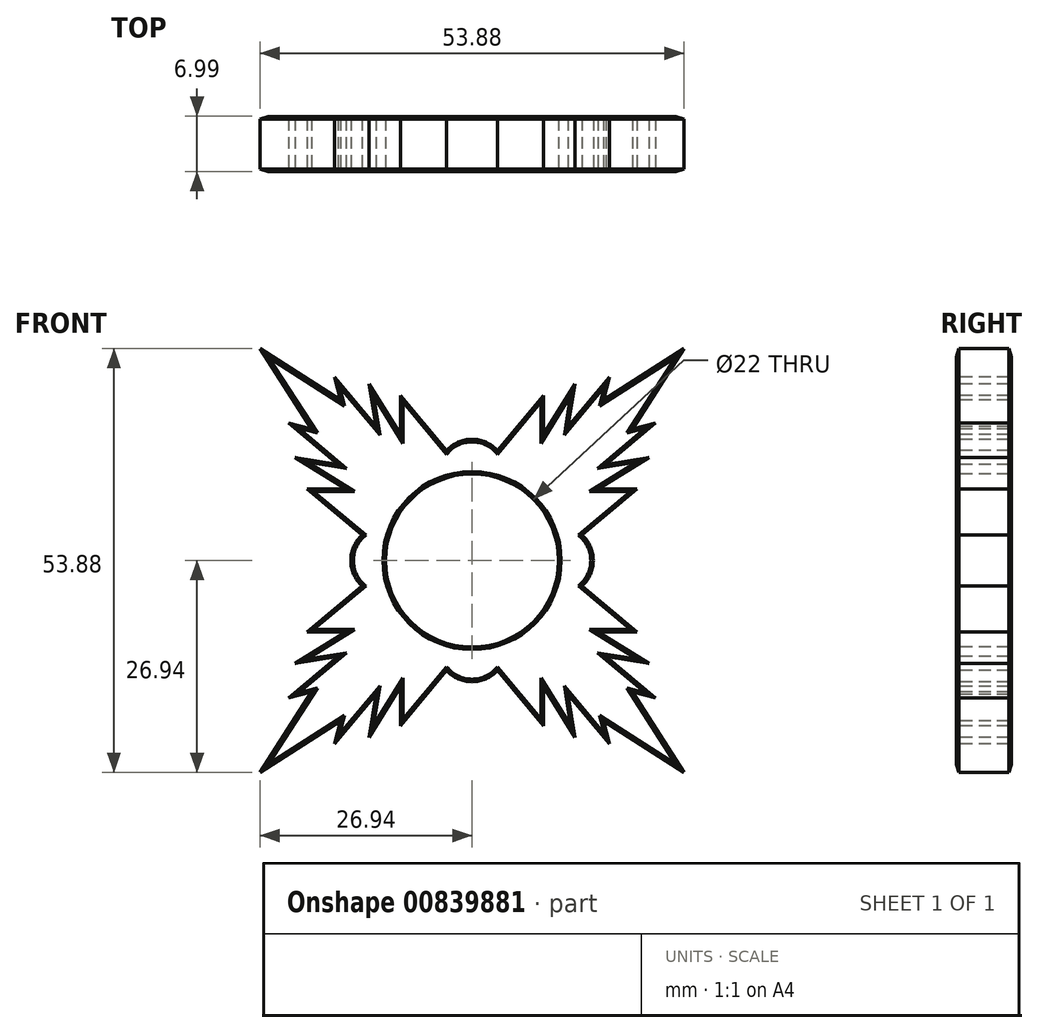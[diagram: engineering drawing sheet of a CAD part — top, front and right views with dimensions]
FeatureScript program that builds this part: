
annotation { "Feature Type Name" : "Feature", "Feature Type Description" : "" }
export const myFeature = defineFeature(function(context is Context, id is Id, definition is map)
    precondition{}
    {
        {
            var Q0;
            Q0=qCreatedBy(makeId("Front.planeOp"),FACE);
            var sketch = newSketch(context, id + "F0", { "sketchPlane" : qUnion([Q0])});
            skLineSegment(sketch, "E0.bottom", {"start": v(26.94, 26.94) * mm, "end": v(-26.94, 26.94) * mm});
            skLineSegment(sketch, "E0.top", {"start": v(26.94, -26.94) * mm, "end": v(-26.94, -26.94) * mm});
            skLineSegment(sketch, "E0.left", {"start": v(26.94, 26.94) * mm, "end": v(26.94, -26.94) * mm});
            skLineSegment(sketch, "E0.right", {"start": v(-26.94, 26.94) * mm, "end": v(-26.94, -26.94) * mm});
            skPoint(sketch, "E0.middle", {"position": v(0, 0) * mm});
            skLineSegment(sketch, "E1", {"start": v(-26.94, 26.94) * mm, "end": v(26.94, -26.94) * mm, "construction": true});
            skLineSegment(sketch, "E2", {"start": v(26.94, 26.94) * mm, "end": v(-26.94, -26.94) * mm, "construction": true});
            skLineSegment(sketch, "E3", {"start": v(0, 26.94) * mm, "end": v(0, -26.94) * mm, "construction": true});
            skLineSegment(sketch, "E4", {"start": v(-26.94, 0) * mm, "end": v(26.94, 0) * mm, "construction": true});
            skCircle(sketch, "E5", {"center": v(0, 0) * mm, "radius": 11 * mm});
            skLineSegment(sketch, "E6", {"start": v(26.94, 26.94) * mm, "end": v(20.36, 16.7) * mm});
            skLineSegment(sketch, "E7", {"start": v(20.36, 16.7) * mm, "end": v(23.3, 17.48) * mm});
            skLineSegment(sketch, "E8", {"start": v(23.3, 17.48) * mm, "end": v(17.02, 12.2) * mm});
            skLineSegment(sketch, "E9", {"start": v(17.02, 12.2) * mm, "end": v(22.45, 13.06) * mm});
            skLineSegment(sketch, "E10", {"start": v(22.45, 13.06) * mm, "end": v(16.02, 9.1) * mm});
            skLineSegment(sketch, "E11", {"start": v(16.02, 9.1) * mm, "end": v(20.98, 9.1) * mm});
            skLineSegment(sketch, "E12", {"start": v(20.98, 9.1) * mm, "end": v(13.98, 3.23) * mm});
            skArc(sketch, "E13", {"start": v(15.4, 0) * mm, "mid": v(15.03, 1.76) * mm, "end": v(13.98, 3.23) * mm});
            skLineSegment(sketch, "E14.MirrorCS", {"start": v(26.94, 26.94) * mm, "end": v(16.7, 20.36) * mm});
            skLineSegment(sketch, "E15.MirrorCS", {"start": v(16.7, 20.36) * mm, "end": v(17.48, 23.3) * mm});
            skLineSegment(sketch, "E16.MirrorCS", {"start": v(17.48, 23.3) * mm, "end": v(12.2, 17.02) * mm});
            skLineSegment(sketch, "E17.MirrorCS", {"start": v(12.2, 17.02) * mm, "end": v(13.06, 22.45) * mm});
            skLineSegment(sketch, "E18.MirrorCS", {"start": v(13.06, 22.45) * mm, "end": v(9.1, 16.02) * mm});
            skLineSegment(sketch, "E19.MirrorCS", {"start": v(9.1, 16.02) * mm, "end": v(9.1, 20.98) * mm});
            skLineSegment(sketch, "E20.MirrorCS", {"start": v(9.1, 20.98) * mm, "end": v(3.23, 13.98) * mm});
            skArc(sketch, "E21.MirrorCS", {"start": v(0, 15.4) * mm, "mid": v(1.76, 15.03) * mm, "end": v(3.23, 13.98) * mm});
            skArc(sketch, "E22.MirrorCS", {"start": v(15.4, 0) * mm, "mid": v(15.03, -1.76) * mm, "end": v(13.98, -3.23) * mm});
            skLineSegment(sketch, "E23.MirrorCS", {"start": v(20.98, -9.1) * mm, "end": v(13.98, -3.23) * mm});
            skLineSegment(sketch, "E24.MirrorCS", {"start": v(16.02, -9.1) * mm, "end": v(20.98, -9.1) * mm});
            skLineSegment(sketch, "E25.MirrorCS", {"start": v(22.45, -13.06) * mm, "end": v(16.02, -9.1) * mm});
            skLineSegment(sketch, "E26.MirrorCS", {"start": v(17.02, -12.2) * mm, "end": v(22.45, -13.06) * mm});
            skLineSegment(sketch, "E27.MirrorCS", {"start": v(23.3, -17.48) * mm, "end": v(17.02, -12.2) * mm});
            skLineSegment(sketch, "E28.MirrorCS", {"start": v(20.36, -16.7) * mm, "end": v(23.3, -17.48) * mm});
            skLineSegment(sketch, "E29.MirrorCS", {"start": v(26.94, -26.94) * mm, "end": v(20.36, -16.7) * mm});
            skLineSegment(sketch, "E30.MirrorCS", {"start": v(26.94, -26.94) * mm, "end": v(16.7, -20.36) * mm});
            skLineSegment(sketch, "E31.MirrorCS", {"start": v(16.7, -20.36) * mm, "end": v(17.48, -23.3) * mm});
            skLineSegment(sketch, "E32.MirrorCS", {"start": v(17.48, -23.3) * mm, "end": v(12.2, -17.02) * mm});
            skLineSegment(sketch, "E33.MirrorCS", {"start": v(12.2, -17.02) * mm, "end": v(13.06, -22.45) * mm});
            skLineSegment(sketch, "E34.MirrorCS", {"start": v(13.06, -22.45) * mm, "end": v(9.1, -16.02) * mm});
            skLineSegment(sketch, "E35.MirrorCS", {"start": v(9.1, -16.02) * mm, "end": v(9.1, -20.98) * mm});
            skLineSegment(sketch, "E36.MirrorCS", {"start": v(9.1, -20.98) * mm, "end": v(3.23, -13.98) * mm});
            skArc(sketch, "E37.MirrorCS", {"start": v(0, -15.4) * mm, "mid": v(1.76, -15.03) * mm, "end": v(3.23, -13.98) * mm});
            skArc(sketch, "E38.MirrorCS", {"start": v(0, 15.4) * mm, "mid": v(-1.76, 15.03) * mm, "end": v(-3.23, 13.98) * mm});
            skLineSegment(sketch, "E39.MirrorCS", {"start": v(-9.1, 20.98) * mm, "end": v(-3.23, 13.98) * mm});
            skLineSegment(sketch, "E40.MirrorCS", {"start": v(-9.1, 16.02) * mm, "end": v(-9.1, 20.98) * mm});
            skLineSegment(sketch, "E41.MirrorCS", {"start": v(-13.06, 22.45) * mm, "end": v(-9.1, 16.02) * mm});
            skLineSegment(sketch, "E42.MirrorCS", {"start": v(-12.2, 17.02) * mm, "end": v(-13.06, 22.45) * mm});
            skLineSegment(sketch, "E43.MirrorCS", {"start": v(-17.48, 23.3) * mm, "end": v(-12.2, 17.02) * mm});
            skLineSegment(sketch, "E44.MirrorCS", {"start": v(-16.7, 20.36) * mm, "end": v(-17.48, 23.3) * mm});
            skLineSegment(sketch, "E45.MirrorCS", {"start": v(-26.94, 26.94) * mm, "end": v(-16.7, 20.36) * mm});
            skLineSegment(sketch, "E46.MirrorCS", {"start": v(-26.94, 26.94) * mm, "end": v(-20.36, 16.7) * mm});
            skLineSegment(sketch, "E47.MirrorCS", {"start": v(-20.36, 16.7) * mm, "end": v(-23.3, 17.48) * mm});
            skLineSegment(sketch, "E48.MirrorCS", {"start": v(-23.3, 17.48) * mm, "end": v(-17.02, 12.2) * mm});
            skLineSegment(sketch, "E49.MirrorCS", {"start": v(-17.02, 12.2) * mm, "end": v(-22.45, 13.06) * mm});
            skLineSegment(sketch, "E50.MirrorCS", {"start": v(-22.45, 13.06) * mm, "end": v(-16.02, 9.1) * mm});
            skLineSegment(sketch, "E51.MirrorCS", {"start": v(-16.02, 9.1) * mm, "end": v(-20.98, 9.1) * mm});
            skLineSegment(sketch, "E52.MirrorCS", {"start": v(-20.98, 9.1) * mm, "end": v(-13.98, 3.23) * mm});
            skArc(sketch, "E53.MirrorCS", {"start": v(-15.4, 0) * mm, "mid": v(-15.03, 1.76) * mm, "end": v(-13.98, 3.23) * mm});
            skArc(sketch, "E54.MirrorCS", {"start": v(-15.4, 0) * mm, "mid": v(-15.03, -1.76) * mm, "end": v(-13.98, -3.23) * mm});
            skLineSegment(sketch, "E55.MirrorCS", {"start": v(-20.98, -9.1) * mm, "end": v(-13.98, -3.23) * mm});
            skLineSegment(sketch, "E56.MirrorCS", {"start": v(-16.02, -9.1) * mm, "end": v(-20.98, -9.1) * mm});
            skLineSegment(sketch, "E57.MirrorCS", {"start": v(-22.45, -13.06) * mm, "end": v(-16.02, -9.1) * mm});
            skLineSegment(sketch, "E58.MirrorCS", {"start": v(-17.02, -12.2) * mm, "end": v(-22.45, -13.06) * mm});
            skLineSegment(sketch, "E59.MirrorCS", {"start": v(-23.3, -17.48) * mm, "end": v(-17.02, -12.2) * mm});
            skLineSegment(sketch, "E60.MirrorCS", {"start": v(-20.36, -16.7) * mm, "end": v(-23.3, -17.48) * mm});
            skLineSegment(sketch, "E61.MirrorCS", {"start": v(-26.94, -26.94) * mm, "end": v(-20.36, -16.7) * mm});
            skLineSegment(sketch, "E62.MirrorCS", {"start": v(-26.94, -26.94) * mm, "end": v(-16.7, -20.36) * mm});
            skLineSegment(sketch, "E63.MirrorCS", {"start": v(-16.7, -20.36) * mm, "end": v(-17.48, -23.3) * mm});
            skLineSegment(sketch, "E64.MirrorCS", {"start": v(-17.48, -23.3) * mm, "end": v(-12.2, -17.02) * mm});
            skLineSegment(sketch, "E65.MirrorCS", {"start": v(-12.2, -17.02) * mm, "end": v(-13.06, -22.45) * mm});
            skLineSegment(sketch, "E66.MirrorCS", {"start": v(-13.06, -22.45) * mm, "end": v(-9.1, -16.02) * mm});
            skLineSegment(sketch, "E67.MirrorCS", {"start": v(-9.1, -16.02) * mm, "end": v(-9.1, -20.98) * mm});
            skLineSegment(sketch, "E68.MirrorCS", {"start": v(-9.1, -20.98) * mm, "end": v(-3.23, -13.98) * mm});
            skArc(sketch, "E69.MirrorCS", {"start": v(0, -15.4) * mm, "mid": v(-1.76, -15.03) * mm, "end": v(-3.23, -13.98) * mm});
            skSolve(sketch);
        }
        {
            var Q0;
            Q0=makeQuery(id+"F0.imprint","IMPRINT",FACE,{"disambiguationData":[TD([[makeQuery(id+"F0.imprint","IMPRINT",EDGE,{"derivedFrom":sQuery(id+"F0.wireOp",EDGE,"E5")}),-1.0]])]});
            extrude(context, id + "F1", {"entities" : qUnion([Q0]), "oppositeDirection" : true, "depth" : 7 * mm, "offsetDistance" : 25.4 * mm});
        }
        {
            var Q0;
            Q0=makeQuery(id+"F1.opExtrude","CAP_FACE",FACE,{"disambiguationData":[OSD([sQuery(id+"F0.wireOp",EDGE,"E5"),sQuery(id+"F0.wireOp",EDGE,"E6"),sQuery(id+"F0.wireOp",EDGE,"E7"),sQuery(id+"F0.wireOp",EDGE,"E8"),sQuery(id+"F0.wireOp",EDGE,"E9"),sQuery(id+"F0.wireOp",EDGE,"E10"),sQuery(id+"F0.wireOp",EDGE,"E11"),sQuery(id+"F0.wireOp",EDGE,"E12"),sQuery(id+"F0.wireOp",EDGE,"E13"),sQuery(id+"F0.wireOp",EDGE,"E14.MirrorCS"),sQuery(id+"F0.wireOp",EDGE,"E15.MirrorCS"),sQuery(id+"F0.wireOp",EDGE,"E16.MirrorCS"),sQuery(id+"F0.wireOp",EDGE,"E17.MirrorCS"),sQuery(id+"F0.wireOp",EDGE,"E18.MirrorCS"),sQuery(id+"F0.wireOp",EDGE,"E19.MirrorCS"),sQuery(id+"F0.wireOp",EDGE,"E20.MirrorCS"),sQuery(id+"F0.wireOp",EDGE,"E21.MirrorCS"),sQuery(id+"F0.wireOp",EDGE,"E22.MirrorCS"),sQuery(id+"F0.wireOp",EDGE,"E23.MirrorCS"),sQuery(id+"F0.wireOp",EDGE,"E24.MirrorCS"),sQuery(id+"F0.wireOp",EDGE,"E25.MirrorCS"),sQuery(id+"F0.wireOp",EDGE,"E26.MirrorCS"),sQuery(id+"F0.wireOp",EDGE,"E27.MirrorCS"),sQuery(id+"F0.wireOp",EDGE,"E28.MirrorCS"),sQuery(id+"F0.wireOp",EDGE,"E29.MirrorCS"),sQuery(id+"F0.wireOp",EDGE,"E30.MirrorCS"),sQuery(id+"F0.wireOp",EDGE,"E31.MirrorCS"),sQuery(id+"F0.wireOp",EDGE,"E32.MirrorCS"),sQuery(id+"F0.wireOp",EDGE,"E33.MirrorCS"),sQuery(id+"F0.wireOp",EDGE,"E34.MirrorCS"),sQuery(id+"F0.wireOp",EDGE,"E35.MirrorCS"),sQuery(id+"F0.wireOp",EDGE,"E36.MirrorCS"),sQuery(id+"F0.wireOp",EDGE,"E37.MirrorCS"),sQuery(id+"F0.wireOp",EDGE,"E38.MirrorCS"),sQuery(id+"F0.wireOp",EDGE,"E39.MirrorCS"),sQuery(id+"F0.wireOp",EDGE,"E40.MirrorCS"),sQuery(id+"F0.wireOp",EDGE,"E41.MirrorCS"),sQuery(id+"F0.wireOp",EDGE,"E42.MirrorCS"),sQuery(id+"F0.wireOp",EDGE,"E43.MirrorCS"),sQuery(id+"F0.wireOp",EDGE,"E44.MirrorCS"),sQuery(id+"F0.wireOp",EDGE,"E45.MirrorCS"),sQuery(id+"F0.wireOp",EDGE,"E46.MirrorCS"),sQuery(id+"F0.wireOp",EDGE,"E47.MirrorCS"),sQuery(id+"F0.wireOp",EDGE,"E48.MirrorCS"),sQuery(id+"F0.wireOp",EDGE,"E49.MirrorCS"),sQuery(id+"F0.wireOp",EDGE,"E50.MirrorCS"),sQuery(id+"F0.wireOp",EDGE,"E51.MirrorCS"),sQuery(id+"F0.wireOp",EDGE,"E52.MirrorCS"),sQuery(id+"F0.wireOp",EDGE,"E53.MirrorCS"),sQuery(id+"F0.wireOp",EDGE,"E54.MirrorCS"),sQuery(id+"F0.wireOp",EDGE,"E55.MirrorCS"),sQuery(id+"F0.wireOp",EDGE,"E56.MirrorCS"),sQuery(id+"F0.wireOp",EDGE,"E57.MirrorCS"),sQuery(id+"F0.wireOp",EDGE,"E58.MirrorCS"),sQuery(id+"F0.wireOp",EDGE,"E59.MirrorCS"),sQuery(id+"F0.wireOp",EDGE,"E60.MirrorCS"),sQuery(id+"F0.wireOp",EDGE,"E61.MirrorCS"),sQuery(id+"F0.wireOp",EDGE,"E62.MirrorCS"),sQuery(id+"F0.wireOp",EDGE,"E63.MirrorCS"),sQuery(id+"F0.wireOp",EDGE,"E64.MirrorCS"),sQuery(id+"F0.wireOp",EDGE,"E65.MirrorCS"),sQuery(id+"F0.wireOp",EDGE,"E66.MirrorCS"),sQuery(id+"F0.wireOp",EDGE,"E67.MirrorCS"),sQuery(id+"F0.wireOp",EDGE,"E68.MirrorCS"),sQuery(id+"F0.wireOp",EDGE,"E69.MirrorCS")])],"isStart":true});
            chamfer(context, id + "F2", {"entities" : qUnion([Q0]), "width" : 0.32 * mm, "tangentPropagation" : true});
        }
        {
            var Q0;
            Q0=makeQuery(id+"F1.opExtrude","CAP_FACE",FACE,{"disambiguationData":[OSD([sQuery(id+"F0.wireOp",EDGE,"E5"),sQuery(id+"F0.wireOp",EDGE,"E6"),sQuery(id+"F0.wireOp",EDGE,"E7"),sQuery(id+"F0.wireOp",EDGE,"E8"),sQuery(id+"F0.wireOp",EDGE,"E9"),sQuery(id+"F0.wireOp",EDGE,"E10"),sQuery(id+"F0.wireOp",EDGE,"E11"),sQuery(id+"F0.wireOp",EDGE,"E12"),sQuery(id+"F0.wireOp",EDGE,"E13"),sQuery(id+"F0.wireOp",EDGE,"E14.MirrorCS"),sQuery(id+"F0.wireOp",EDGE,"E15.MirrorCS"),sQuery(id+"F0.wireOp",EDGE,"E16.MirrorCS"),sQuery(id+"F0.wireOp",EDGE,"E17.MirrorCS"),sQuery(id+"F0.wireOp",EDGE,"E18.MirrorCS"),sQuery(id+"F0.wireOp",EDGE,"E19.MirrorCS"),sQuery(id+"F0.wireOp",EDGE,"E20.MirrorCS"),sQuery(id+"F0.wireOp",EDGE,"E21.MirrorCS"),sQuery(id+"F0.wireOp",EDGE,"E22.MirrorCS"),sQuery(id+"F0.wireOp",EDGE,"E23.MirrorCS"),sQuery(id+"F0.wireOp",EDGE,"E24.MirrorCS"),sQuery(id+"F0.wireOp",EDGE,"E25.MirrorCS"),sQuery(id+"F0.wireOp",EDGE,"E26.MirrorCS"),sQuery(id+"F0.wireOp",EDGE,"E27.MirrorCS"),sQuery(id+"F0.wireOp",EDGE,"E28.MirrorCS"),sQuery(id+"F0.wireOp",EDGE,"E29.MirrorCS"),sQuery(id+"F0.wireOp",EDGE,"E30.MirrorCS"),sQuery(id+"F0.wireOp",EDGE,"E31.MirrorCS"),sQuery(id+"F0.wireOp",EDGE,"E32.MirrorCS"),sQuery(id+"F0.wireOp",EDGE,"E33.MirrorCS"),sQuery(id+"F0.wireOp",EDGE,"E34.MirrorCS"),sQuery(id+"F0.wireOp",EDGE,"E35.MirrorCS"),sQuery(id+"F0.wireOp",EDGE,"E36.MirrorCS"),sQuery(id+"F0.wireOp",EDGE,"E37.MirrorCS"),sQuery(id+"F0.wireOp",EDGE,"E38.MirrorCS"),sQuery(id+"F0.wireOp",EDGE,"E39.MirrorCS"),sQuery(id+"F0.wireOp",EDGE,"E40.MirrorCS"),sQuery(id+"F0.wireOp",EDGE,"E41.MirrorCS"),sQuery(id+"F0.wireOp",EDGE,"E42.MirrorCS"),sQuery(id+"F0.wireOp",EDGE,"E43.MirrorCS"),sQuery(id+"F0.wireOp",EDGE,"E44.MirrorCS"),sQuery(id+"F0.wireOp",EDGE,"E45.MirrorCS"),sQuery(id+"F0.wireOp",EDGE,"E46.MirrorCS"),sQuery(id+"F0.wireOp",EDGE,"E47.MirrorCS"),sQuery(id+"F0.wireOp",EDGE,"E48.MirrorCS"),sQuery(id+"F0.wireOp",EDGE,"E49.MirrorCS"),sQuery(id+"F0.wireOp",EDGE,"E50.MirrorCS"),sQuery(id+"F0.wireOp",EDGE,"E51.MirrorCS"),sQuery(id+"F0.wireOp",EDGE,"E52.MirrorCS"),sQuery(id+"F0.wireOp",EDGE,"E53.MirrorCS"),sQuery(id+"F0.wireOp",EDGE,"E54.MirrorCS"),sQuery(id+"F0.wireOp",EDGE,"E55.MirrorCS"),sQuery(id+"F0.wireOp",EDGE,"E56.MirrorCS"),sQuery(id+"F0.wireOp",EDGE,"E57.MirrorCS"),sQuery(id+"F0.wireOp",EDGE,"E58.MirrorCS"),sQuery(id+"F0.wireOp",EDGE,"E59.MirrorCS"),sQuery(id+"F0.wireOp",EDGE,"E60.MirrorCS"),sQuery(id+"F0.wireOp",EDGE,"E61.MirrorCS"),sQuery(id+"F0.wireOp",EDGE,"E62.MirrorCS"),sQuery(id+"F0.wireOp",EDGE,"E63.MirrorCS"),sQuery(id+"F0.wireOp",EDGE,"E64.MirrorCS"),sQuery(id+"F0.wireOp",EDGE,"E65.MirrorCS"),sQuery(id+"F0.wireOp",EDGE,"E66.MirrorCS"),sQuery(id+"F0.wireOp",EDGE,"E67.MirrorCS"),sQuery(id+"F0.wireOp",EDGE,"E68.MirrorCS"),sQuery(id+"F0.wireOp",EDGE,"E69.MirrorCS")])],"isStart":false});
            chamfer(context, id + "F3", {"entities" : qUnion([Q0]), "width" : 0.32 * mm, "tangentPropagation" : true});
        }
    });
